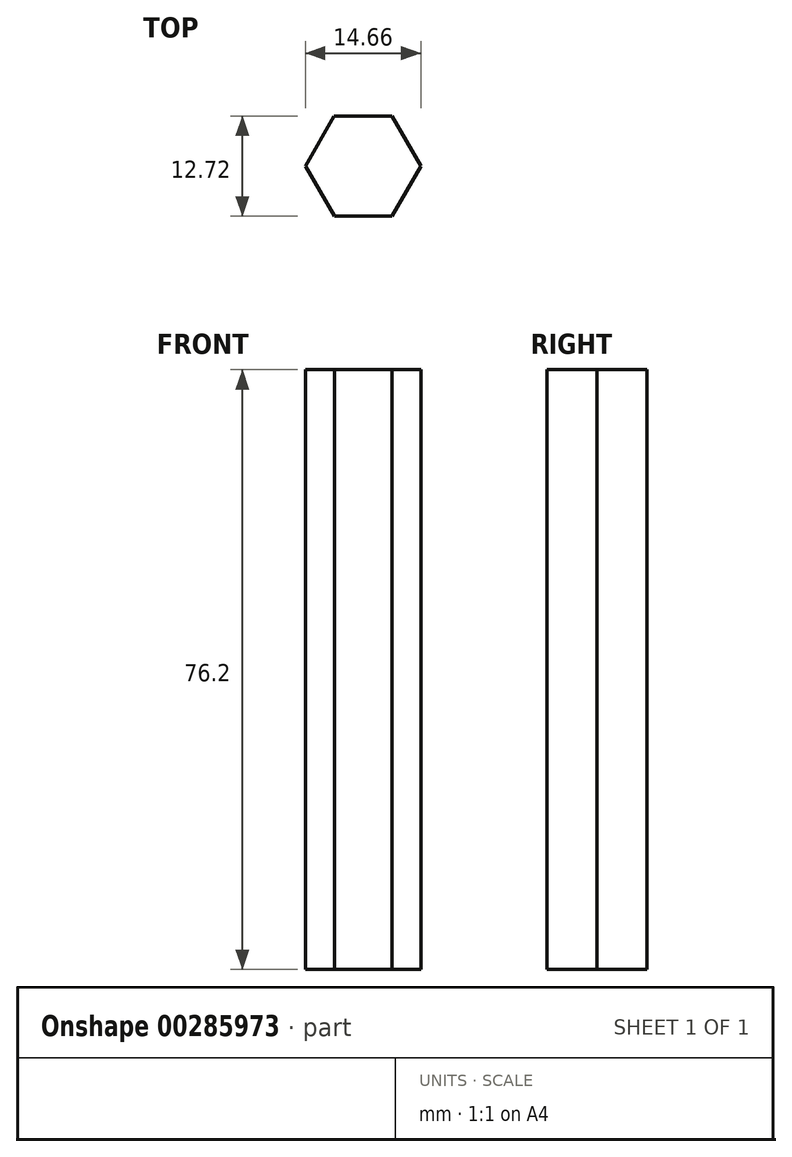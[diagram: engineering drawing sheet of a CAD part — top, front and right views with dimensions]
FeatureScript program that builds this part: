
annotation { "Feature Type Name" : "Feature", "Feature Type Description" : "" }
export const myFeature = defineFeature(function(context is Context, id is Id, definition is map)
    precondition{}
    {
        {
            var Q0;
            Q0=qCreatedBy(makeId("Top.planeOp"),FACE);
            var sketch = newSketch(context, id + "F0", { "sketchPlane" : qUnion([Q0])});
            skCircle(sketch, "E0.cCircle", {"center": v(0, 0) * mm, "radius": 6.35 * mm, "construction": true});
            skLineSegment(sketch, "E0.0", {"start": v(-7.33, -0.01) * mm, "end": v(-3.68, 6.34) * mm});
            skLineSegment(sketch, "E0.1", {"start": v(-3.68, 6.34) * mm, "end": v(3.66, 6.36) * mm});
            skLineSegment(sketch, "E0.2", {"start": v(3.66, 6.36) * mm, "end": v(7.33, 0.01) * mm});
            skLineSegment(sketch, "E0.3", {"start": v(7.33, 0.01) * mm, "end": v(3.68, -6.34) * mm});
            skLineSegment(sketch, "E0.4", {"start": v(3.68, -6.34) * mm, "end": v(-3.66, -6.36) * mm});
            skLineSegment(sketch, "E0.5", {"start": v(-3.66, -6.36) * mm, "end": v(-7.33, -0.01) * mm});
            skPoint(sketch, "E0.0.midPoint", {"position": v(-5.5, 3.17) * mm});
            skSolve(sketch);
        }
        {
            var Q0;
            Q0 = qSketchRegion(id + "F0", true);
            extrude(context, id + "F1", {"entities" : qUnion([Q0]), "depth" : 76.2 * mm});
        }
    });
